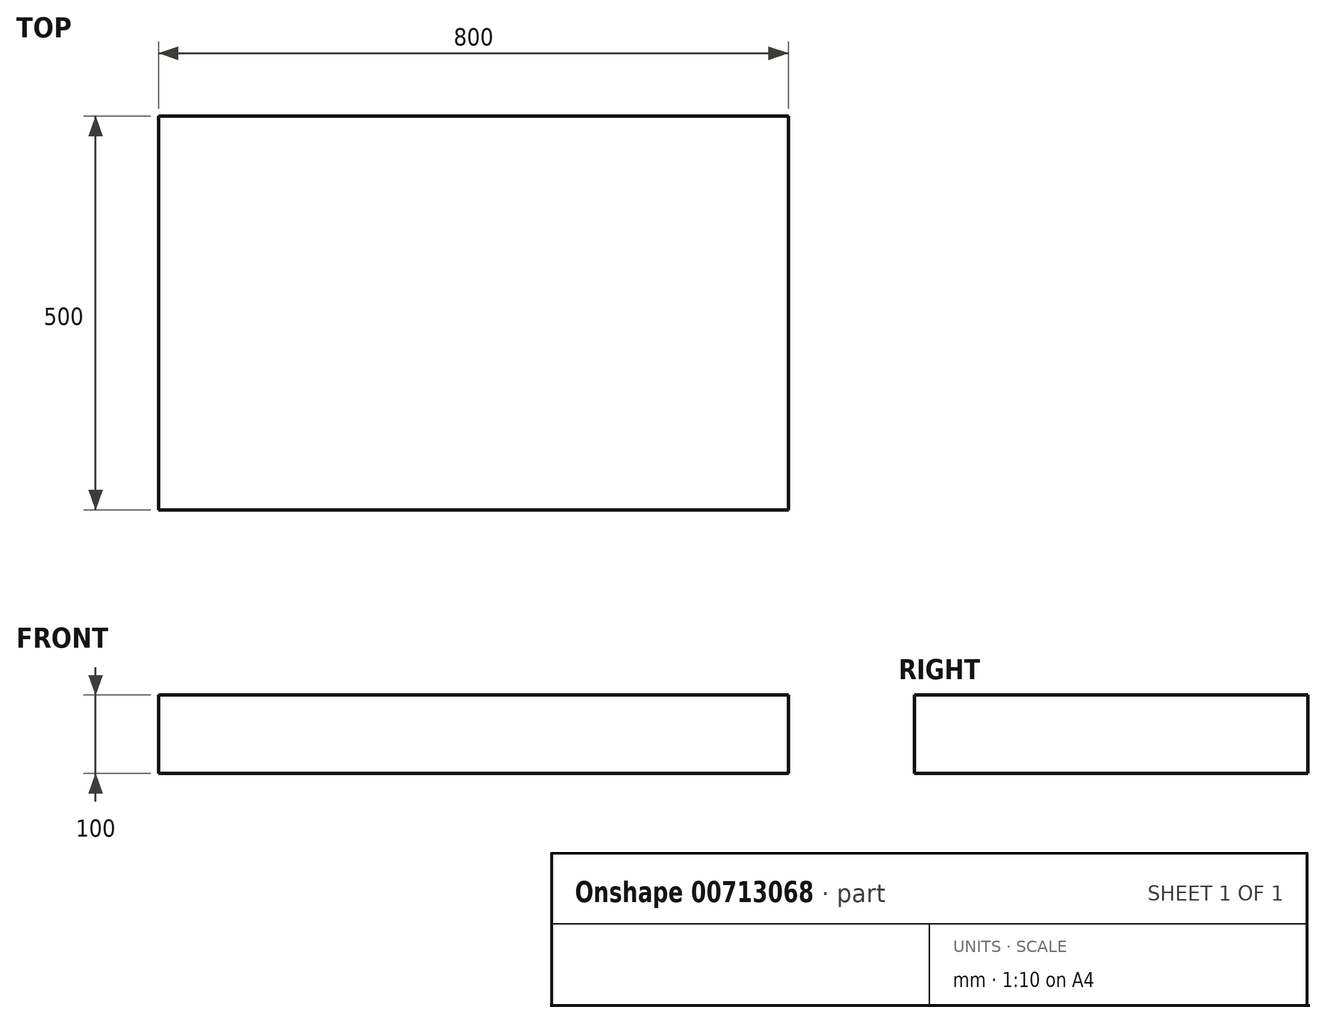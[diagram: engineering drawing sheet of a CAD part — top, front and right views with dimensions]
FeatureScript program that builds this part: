
annotation { "Feature Type Name" : "Feature", "Feature Type Description" : "" }
export const myFeature = defineFeature(function(context is Context, id is Id, definition is map)
    precondition{}
    {
        {
            var Q0;
            Q0=qCreatedBy(makeId("Right.planeOp"),FACE);
            var sketch = newSketch(context, id + "F0", { "sketchPlane" : qUnion([Q0])});
            skLineSegment(sketch, "E0", {"start": v(-174.82, 69.83) * mm, "end": v(325.18, 69.83) * mm});
            skLineSegment(sketch, "E1", {"start": v(325.18, 69.83) * mm, "end": v(325.18, -30.17) * mm});
            skLineSegment(sketch, "E2", {"start": v(325.18, -30.17) * mm, "end": v(-174.82, -30.17) * mm});
            skLineSegment(sketch, "E3", {"start": v(-174.82, -30.17) * mm, "end": v(-174.82, 69.83) * mm});
            skSolve(sketch);
        }
        {
            var Q0;
            Q0=makeQuery(id+"F0.imprint","IMPRINT",FACE,{"disambiguationData":[TD([[makeQuery(id+"F0.imprint","IMPRINT",EDGE,{"derivedFrom":sQuery(id+"F0.wireOp",EDGE,"E0")}),-1.0]])]});
            extrude(context, id + "F1", {"entities" : qUnion([Q0]), "depth" : 800 * mm, "offsetDistance" : 25 * mm});
        }
    });
